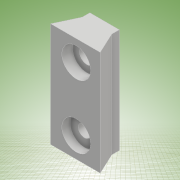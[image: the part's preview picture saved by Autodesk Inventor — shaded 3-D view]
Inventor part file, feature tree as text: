
AUTODESK INVENTOR PART (.ipt)
format: ipt  version: 2017 (Build 210142000, 142)  size: 135,168 bytes
history: native  units: mm
features: hole x2, extrude x1, sketch x1
ambient origin geometry x8: Origin, YZ Plane, XZ Plane, XY Plane, X Axis, Y Axis, Z Axis, Center Point
bodies: Solid1 (feature_tree)
feature tree (4):
  extrude  "Extrusion1"  Depth=2.0mm
  hole  "Hole1"  [1 undecoded]
  hole  "Hole2"  [1 undecoded]
  sketch  "Sketch1"  dims[d4=25.4mm d5=0.0mm d6=5.842mm d30=5.0mm d8=3.6mm d9=6.0mm d10=7.0mm d11=2.6mm d12=90.0deg d13=8.0mm d14=20.594885mm d20=12.7mm d22=5.5mm d23=5.5mm d24=2.0mm d25=2.0mm d28=0.2mm d29=27.052603mm d31=27.052603mm d32=5.842mm d33=5.0mm d34=3.0mm d35=6.0mm d36=7.0mm d37=2.0mm d38=90.0deg d39=8.0mm d40=20.594885mm]
note: 2 required parameter values undecoded (feature->parameter linkage not recoverable at this tier; creation-order binding heuristic only, values carry confidence <= 0.55)
